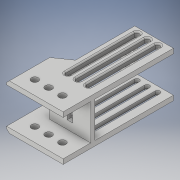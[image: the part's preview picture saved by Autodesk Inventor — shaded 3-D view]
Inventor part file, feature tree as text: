
AUTODESK INVENTOR PART (.ipt)
format: ipt  version: 2019 (Build 230136000, 136)  size: 449,536 bytes
history: native  units: mm
features: extrude x14, sketch x14, projected_geometry x6, mirror x4, plane x2, chamfer x2, fillet x1
ambient origin geometry x8: Origin, YZ Plane, XZ Plane, XY Plane, X Axis, Y Axis, Z Axis, Center Point
bodies: Solid1 (feature_tree)
feature tree (43):
  extrude  "Extrusion1"  Depth=30.0mm
  extrude  "Extrusion2"  Depth=2.0mm
  extrude  "Extrusion3"  Depth=2.0mm
  extrude  "Extrusion4"  Depth=28.0mm TaperAngle=0.0deg
  extrude  "Extrusion5"  Depth=41.0mm
  extrude  "Extrusion6"  Depth=20.0mm TaperAngle=0.0deg
  extrude  "Extrusion7"  Depth=2.0mm TaperAngle=0.0deg
  plane  "Work Plane1"
  sketch  "Sketch8"  dims[d27=20.0mm d28=0.0mm d36=50.0mm d37=0.0mm]
  mirror  "Mirror1"
  mirror  "Mirror2"
  extrude  "Extrusion9"  Depth=20.0mm TaperAngle=0.0deg
  extrude  "Extrusion10"  Depth=10.0mm TaperAngle=0.0deg
  extrude  "Extrusion12"  Depth=1.5mm TaperAngle=0.0deg
  sketch  "Sketch12"  dims[d53=1.0mm d54=0.0mm d55=1.5mm d56=0.0mm]
  plane  "Work Plane3"
  extrude  "Extrusion13"  Depth=1.5mm TaperAngle=0.0deg
  mirror  "Mirror4"
  extrude  "Extrusion14"  Depth=2.0mm TaperAngle=45.0deg
  extrude  "Extrusion15"  Depth=1.0mm TaperAngle=0.0deg
  chamfer  "Chamfer1"  [1 undecoded]
  chamfer  "Chamfer2"  [1 undecoded]
  fillet  "Fillet4"  [1 undecoded]
  mirror  "Mirror6"
  extrude  "Extrusion17"  [1 undecoded]
  sketch  "Sketch1"  dims[d0=30.0mm d1=58.0mm]
  sketch  "Sketch2"  dims[d2=2.0mm d3=2.0mm]
  projected_geometry  "Projected Loop1"
  sketch  "Sketch3"  dims[d4=2.0mm d5=0.0mm d6=2.0mm]
  sketch  "Sketch4"  dims[d7=28.0mm d8=0.0mm d9=28.0mm d10=0.0mm]
  sketch  "Sketch5"  dims[d13=28.0mm d14=0.0mm d15=41.0mm]
  sketch  "Sketch6"  dims[d16=2.0mm d17=20.0mm d18=18.0mm d19=0.0mm d20=0.0mm]
  sketch  "Sketch7"  dims[d21=7.5mm d25=2.0mm d26=0.0mm]
  projected_geometry  "Projected Loop2"
  sketch  "Sketch9"  dims[d40=0.1mm d41=10.0mm d42=0.0mm]
  sketch  "Sketch11"  dims[d49=200.0mm d50=0.0mm d51=1.5mm d52=0.0mm]
  projected_geometry  "Projected Loop4"
  sketch  "Sketch13"  dims[d59=2.0mm d60=2.0mm d61=45.0deg d62=2.0mm d63=2.0mm d64=45.0deg]
  projected_geometry  "Projected Loop5"
  sketch  "Sketch14"  dims[d65=1.0mm d66=0.5mm d67=0.0mm]
  projected_geometry  "Projected Loop6"
  sketch  "Sketch16"
  projected_geometry  "Projected Loop8"
note: 4 required parameter values undecoded (feature->parameter linkage not recoverable at this tier; creation-order binding heuristic only, values carry confidence <= 0.55)
